# Revit family: UM377 Banco Quatro
name_source: partatom
category: Mobiliario
units: mm (PartAtom-declared; Revit-internal decimal feet)

## family parameters
Compartido = No
Corte con vacíos al cargar = No
Número OmniClass = 23.40.20.00
Punto de cálculo de habitación = No
Se basa en plano de trabajo = No
Siempre vertical = Sí
Título OmniClass = General Furniture and Specialties

## types (1)
- UM377X Banco Quatro
    Acabado Listones = Lignus, protector fungicida, insecticida e hidrófugo.
    Acabado bancada = Pies de acero con imprimacion epoxi y acabado en oxirón rojo óxido.
    Accessibilidad = Sí
    Altura asiento = 450 mm  [stored 1.47638 ft]
    Altura total = 795 mm  [stored 2.60827 ft]
    Ancho = 665 mm  [stored 2.18176 ft]
    Comentarios de tipo = Pies de acero con imprimacion epoxi y acabado en oxirón rojo óxido y cinco tablones de sección 140 x 70mm de madera tropical
tratada con Lignus protector fungicida, insecticida e hidrófugo. Acabado en color natural.
    Fabricante = BENITO
    Ficha tecnica = http://www.benito.com
    Instalación = Anclaje recomendado: Tornillos M10 roscados a las bancadas y embebidos en hormigón.Tornillos no suministrados.
    Largo = 2000 mm  [stored 6.56168 ft]
    Material bancada = Fundición dúctil
    Material listones = Madera Tropical
    Modelo = Banco Quatro
    Referencia = UM377X
    URL = http://www.benito.com
    URL Producto = http://www.benito.com

note: [stored X ft] marks values corroborated as IEEE doubles in the binary element streams (Revit-internal decimal feet)

## geometry (parser evidence)
native form markers: Blend x4
no freeform markers — native parametric forms only
